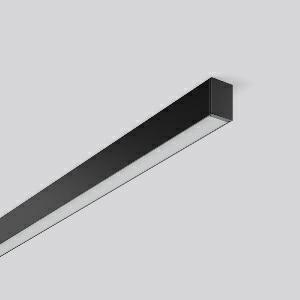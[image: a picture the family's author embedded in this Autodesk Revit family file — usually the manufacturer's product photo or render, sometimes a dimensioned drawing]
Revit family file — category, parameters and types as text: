
# Revit family: less_is_more_27_312201_003_9de7
name_source: partatom
category: Lighting Fixtures
units: mm (PartAtom-declared; Revit-internal decimal feet)

## family parameters
Cut with Voids When Loaded = No
Host = Face
Light Source = No
Part Type = Normal
Room Calculation Point = No
Round Connector Dimension = Use Diameter
Shared = No

## types (1)
- LESS IS MORE 27 (1 x LED Modul 830, 2750 lm, 3000)
    Apparent Load = 43 VA
    CIE Flux Codes = 65 89 98 100 100
    Color Rendering = 80
    Color Temperature = 3000
    Default Elevation = 1800 mm
    Description = Series: LESS IS MORE 27
Ceiling luminaire with slim design. Housing: extruded aluminium profile, powder-coated. End cap aluminium powder-coated. Diffuser made of non-yellowing plastic (PMMA) microprismatic. Suitable for Ceiling mounting, Wall (surface). External driver with connecting cable. 
Colour: deep black, matt (RAL 9005)
Length: 1512 mm
Width: 28 mm
Height: 38 mm
Lamp: LED
Socket: without socket
Colour temperature: 3000K
Colour rendering index (CRI): 82
System power: 43 W
Rated luminous flux: 2750 lm
Luminous efficiency: 64 lm/W
Control gear: Regulated power supply
Protection class: II
Type of protection: IP 20
    Height = 38 mm
    Lamp = 1 x LED Modul 830
    Lamp Light Flux = 2750 lm
    Lamp count = 1
    Length = 1512 mm
    Lifetime = 50000 h
    Luminous efficacy = 64 lm/W
    Manufacturer = RZB
    ModVariant = No
    Model = 312201.003
    Mounting Place = Ceiling, Wall
    Mounting Type = Surface mounted
    Number of Poles = 1
    OnlyDefault = Yes
    Power Factor = 1
    Product Name = LESS IS MORE 27
    Product group = Surface mounted LED linear luminaires
    ProductGroupID = 307
    Protection Class = Protection class II
    Protection Degree = IP 20
    RLX_Detail_Level = 1
    RLX_Emergency_Light_Flux = 0 lm
    RLX_Emergency_Type = 0
    RLX_Emergency_Type_DB = No
    RlxData = <blob elided: 29797 chars, md5=912e4a90>
    Socket = socket
    Standby Power = 0 W
    System Light Flux = 2750 lm
    System Power = 43 W
    Type Comments = Product without accessories
    Type Image = 312197.003.jpg
    URL = http://relux.com
    VarID = ---
    Voltage = 230 V
    Voltage Range = 220-240 V
    Weight = 0.00 kg
    Width = 28 mm

## geometry (parser evidence)
native form markers: Blend x4, Sweep x11
no freeform markers — native parametric forms only
